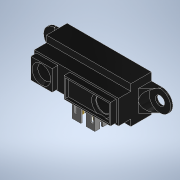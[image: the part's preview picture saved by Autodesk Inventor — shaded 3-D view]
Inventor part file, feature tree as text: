
AUTODESK INVENTOR PART (.ipt)
format: ipt  version: 2022.3 (Build 263350000, 350)  size: 229,888 bytes
history: mixed  units: mm (DEFAULTED — no unit token found)
features: other x4, revolve x2, chamfer x2, imported_body x1
ambient origin geometry x8: Origin, YZ Plane, XZ Plane, XY Plane, X Axis, Y Axis, Z Axis, Center Point
bodies: Solid1 (imported_parasolid), Solid2 (imported_parasolid), Solid3 (imported_parasolid), Solid4 (imported_parasolid), Solid5 (imported_parasolid), Solid6 (imported_parasolid), Solid7 (imported_parasolid), Solid8 (imported_parasolid)
feature tree (9):
  revolve  "Revolve1"  [1 undecoded]
  chamfer  "Chamfer2"  [1 undecoded]
  revolve  "Revolve2"  [1 undecoded]
  other  "Boss-Extrude8"
  other  "Cut-Extrude13"
  chamfer  "Chamfer3"  [1 undecoded]
  other  "LPattern1[1]"
  other  "LPattern1[2]"
  imported_body  NMx_Import_Brep_tag  [imported B-rep: ~47 faces, bbox_mm=[31.95, 15.6, 11.75]]
note: 4 required parameter values undecoded (feature->parameter linkage not recoverable at this tier; creation-order binding heuristic only, values carry confidence <= 0.55)
